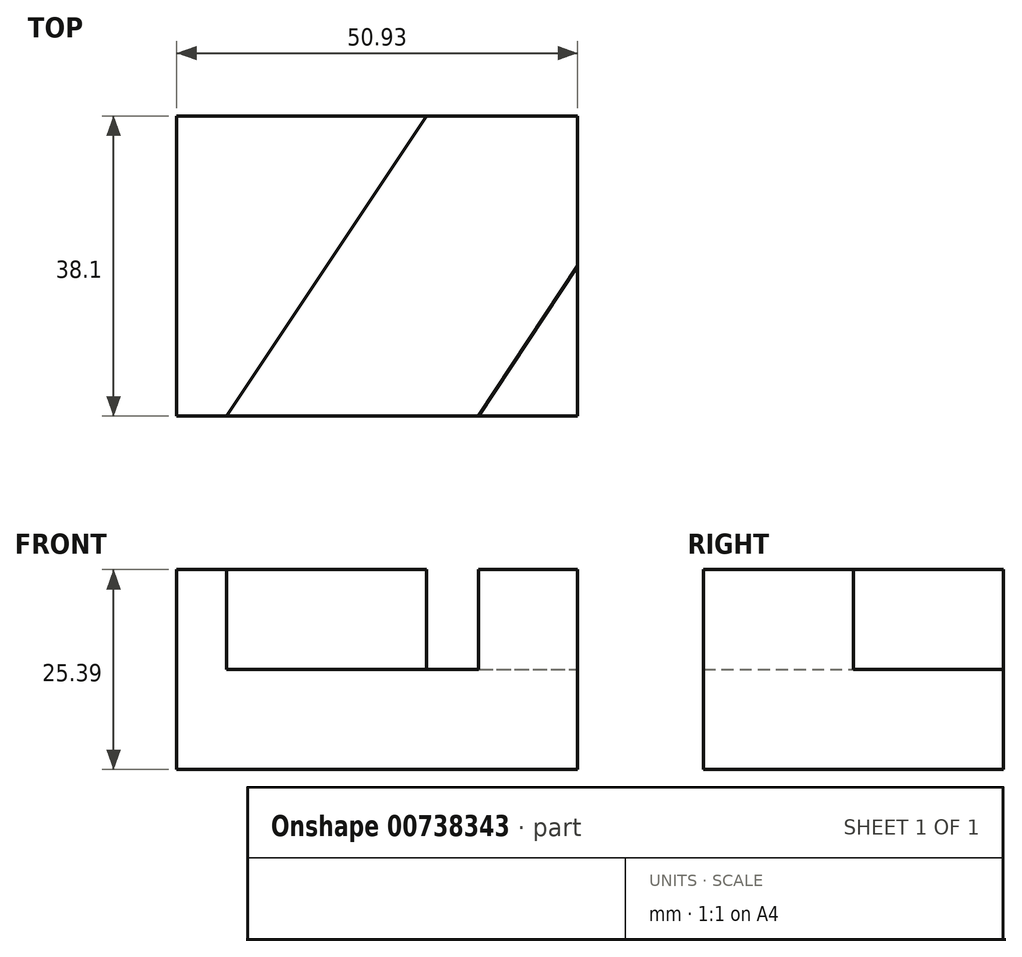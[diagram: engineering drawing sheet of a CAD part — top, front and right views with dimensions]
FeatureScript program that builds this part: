
annotation { "Feature Type Name" : "Feature", "Feature Type Description" : "" }
export const myFeature = defineFeature(function(context is Context, id is Id, definition is map)
    precondition{}
    {
        {
            var Q0;
            Q0=qCreatedBy(makeId("Front.planeOp"),FACE);
            var sketch = newSketch(context, id + "F0", { "sketchPlane" : qUnion([Q0])});
            skLineSegment(sketch, "E0", {"start": v(0, 0) * mm, "end": v(0, 25.4) * mm});
            skLineSegment(sketch, "E1", {"start": v(0, 25.4) * mm, "end": v(50.93, 25.4) * mm});
            skLineSegment(sketch, "E2", {"start": v(50.93, 25.4) * mm, "end": v(50.93, 0) * mm});
            skLineSegment(sketch, "E3", {"start": v(50.93, 0) * mm, "end": v(0, 0) * mm});
            skSolve(sketch);
        }
        {
            var Q0;
            Q0 = qSketchRegion(id + "F0", true);
            extrude(context, id + "F1", {"entities" : qUnion([Q0]), "depth" : 38.1 * mm, "offsetDistance" : 25.4 * mm});
        }
        {
            var Q0;
            Q0=makeQuery(id+"F1.opExtrude","SWEPT_FACE",FACE,{"disambiguationData":[OSD([sQuery(id+"F0.wireOp",EDGE,"E1")])]});
            var sketch = newSketch(context, id + "F2", { "sketchPlane" : qUnion([Q0])});
            skLineSegment(sketch, "E4", {"start": v(0, -38.1) * mm, "end": v(6.35, -38.1) * mm});
            skLineSegment(sketch, "E5", {"start": v(6.35, -38.1) * mm, "end": v(31.75, 0) * mm});
            skLineSegment(sketch, "E6", {"start": v(31.75, 0) * mm, "end": v(0, 0) * mm});
            skLineSegment(sketch, "E7", {"start": v(50.93, -38.1) * mm, "end": v(38.34, -38.1) * mm});
            skLineSegment(sketch, "E8", {"start": v(38.34, -38.1) * mm, "end": v(50.93, -19.05) * mm});
            skLineSegment(sketch, "E9", {"start": v(50.93, -19.05) * mm, "end": v(50.93, -38.1) * mm});
            skLineSegment(sketch, "E10", {"start": v(31.75, 0) * mm, "end": v(50.93, 0) * mm});
            skLineSegment(sketch, "E11", {"start": v(50.93, 0) * mm, "end": v(50.93, -19.05) * mm});
            skLineSegment(sketch, "E12", {"start": v(38.34, -38.1) * mm, "end": v(6.35, -38.1) * mm});
            skSolve(sketch);
        }
        {
            var Q0;
            Q0=makeQuery(id+"F2.imprint","IMPRINT",FACE,{"disambiguationData":[TD([[makeQuery(id+"F2.imprint","IMPRINT",EDGE,{"derivedFrom":sQuery(id+"F2.wireOp",EDGE,"E5")}),-1.0]])]});
            extrude(context, id + "F3", {"entities" : qUnion([Q0]), "operationType" : NewBodyOperationType.REMOVE, "oppositeDirection" : true, "depth" : 12.7 * mm, "offsetDistance" : 25.4 * mm});
        }
    });
